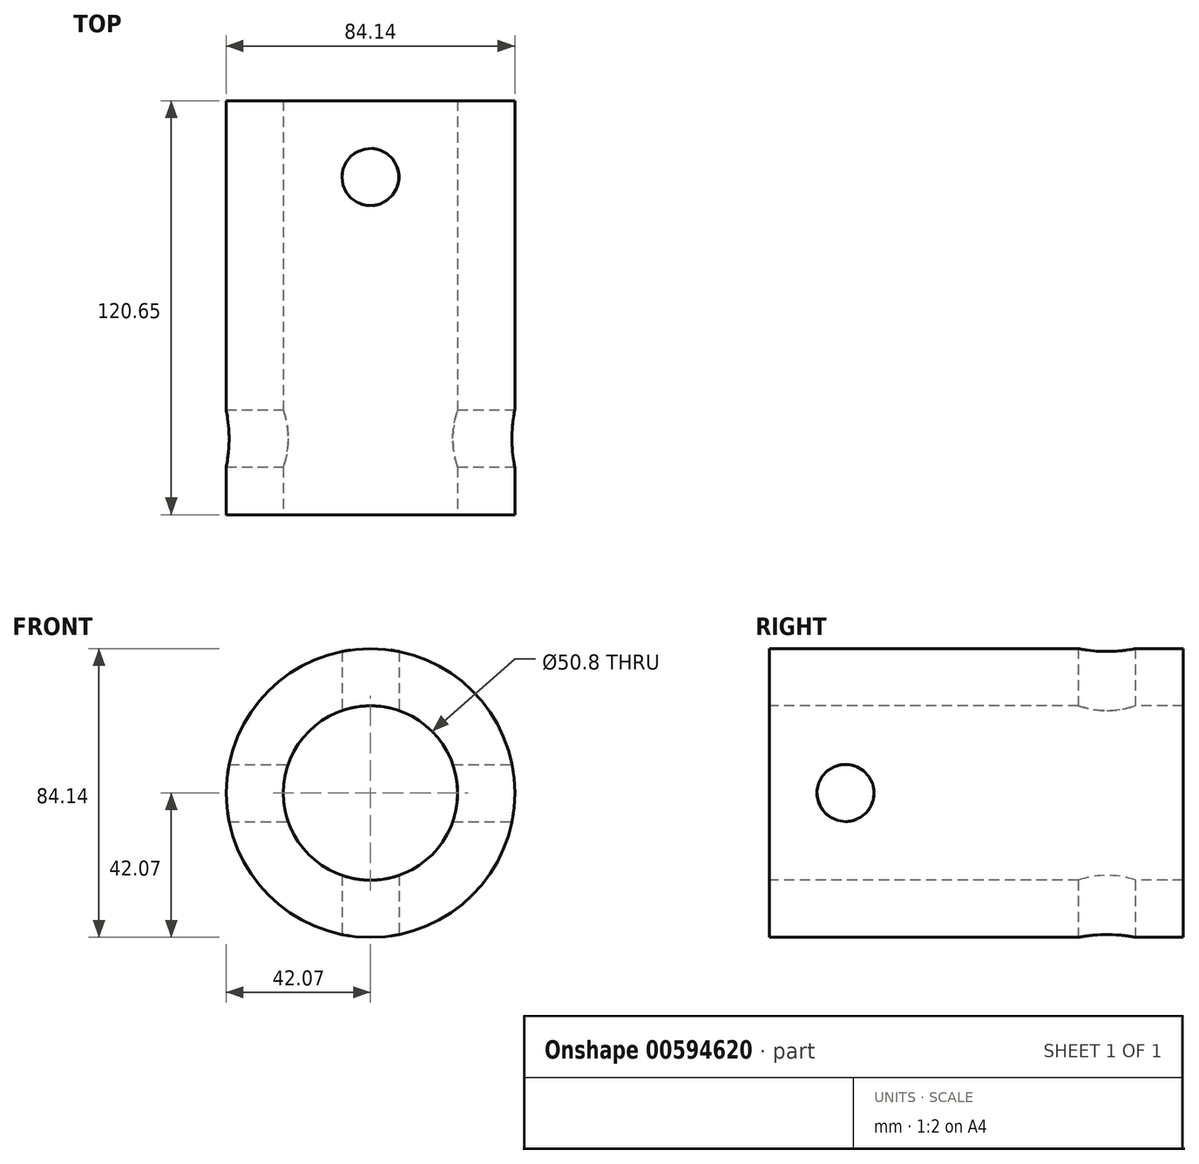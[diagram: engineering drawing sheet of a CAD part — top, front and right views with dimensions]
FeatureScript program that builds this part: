
annotation { "Feature Type Name" : "Feature", "Feature Type Description" : "" }
export const myFeature = defineFeature(function(context is Context, id is Id, definition is map)
    precondition{}
    {
        {
            var Q0;
            Q0=qCreatedBy(makeId("Front.planeOp"),FACE);
            var sketch = newSketch(context, id + "F0", { "sketchPlane" : qUnion([Q0])});
            skCircle(sketch, "E0", {"center": v(0, 0) * mm, "radius": 42.07 * mm});
            skCircle(sketch, "E1", {"center": v(0, 0) * mm, "radius": 25.4 * mm});
            skSolve(sketch);
        }
        {
            var Q0;
            Q0=makeQuery(id+"F0.imprint","IMPRINT",FACE,{"disambiguationData":[TD([[makeQuery(id+"F0.imprint","IMPRINT",EDGE,{"derivedFrom":sQuery(id+"F0.wireOp",EDGE,"E0")}),1.0]])]});
            extrude(context, id + "F1", {"entities" : qUnion([Q0]), "oppositeDirection" : true, "depth" : 120.65 * mm, "offsetDistance" : 25.4 * mm});
        }
        {
            var Q0;
            Q0=qCreatedBy(makeId("Right.planeOp"),FACE);
            var sketch = newSketch(context, id + "F2", { "sketchPlane" : qUnion([Q0])});
            skCircle(sketch, "E2", {"center": v(22.23, 0) * mm, "radius": 8.33 * mm});
            skSolve(sketch);
        }
        {
            var Q0;
            Q0=makeQuery(id+"F2.imprint","IMPRINT",FACE,{"disambiguationData":[TD([[makeQuery(id+"F2.imprint","IMPRINT",EDGE,{"derivedFrom":sQuery(id+"F2.wireOp",EDGE,"E2")}),1.0]])]});
            extrude(context, id + "F3", {"entities" : qUnion([Q0]), "operationType" : NewBodyOperationType.REMOVE, "endBound" : BoundingType.SYMMETRIC, "oppositeDirection" : true, "depth" : 127 * mm, "offsetDistance" : 25.4 * mm});
        }
        {
            var Q0;
            Q0=qCreatedBy(makeId("Top.planeOp"),FACE);
            var sketch = newSketch(context, id + "F4", { "sketchPlane" : qUnion([Q0])});
            skCircle(sketch, "E3", {"center": v(0, 98.43) * mm, "radius": 8.33 * mm});
            skSolve(sketch);
        }
        {
            var Q0;
            Q0=makeQuery(id+"F4.imprint","IMPRINT",FACE,{"disambiguationData":[TD([[makeQuery(id+"F4.imprint","IMPRINT",EDGE,{"derivedFrom":sQuery(id+"F4.wireOp",EDGE,"E3")}),1.0]])]});
            extrude(context, id + "F5", {"entities" : qUnion([Q0]), "operationType" : NewBodyOperationType.REMOVE, "endBound" : BoundingType.SYMMETRIC, "depth" : 101.6 * mm, "offsetDistance" : 25.4 * mm});
        }
    });
